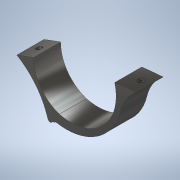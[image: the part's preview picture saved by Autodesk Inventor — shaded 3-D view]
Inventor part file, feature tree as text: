
AUTODESK INVENTOR PART (.ipt)
format: ipt  version: 2021 (Build 250183000, 183)  size: 151,040 bytes
history: native  units: in
note: dims shown in document units (in); Inventor stores cm internally (conversion verified against a paired STEP export)
features: extrude x3, plane x2, thread x2, other x1, sketch x1
ambient origin geometry x8: Origin, YZ Plane, XZ Plane, XY Plane, X Axis, Y Axis, Z Axis, Center Point
bodies: Solid1 (feature_tree)
feature tree (9):
  extrude  "Extrusion1"  Depth=0.3937in
  plane  "Work Plane1"
  extrude  "Extrusion2"  Depth=0.3937in TaperAngle=0.0deg
  thread  "Thread1"  [1 undecoded]
  plane  "Work Plane2"
  extrude  "Extrusion3"  Depth=0.3937in
  thread  "Thread2"  [1 undecoded]
  other  "Eixo de trabalho1"
  sketch  "Sketch1"  dims[d0=0.3535in d1=0.0in d2=0.0787in d3=0.3563in d4=0.0in d5=0.3937in d6=0.0in d7=0.0787in d8=0.3563in d9=0.0in d10=0.3937in d11=0.0in d12=0.1181in d13=0.1781in d14=0.3535in d15=0.1781in d16=0.1106in]
note: 2 required parameter values undecoded (feature->parameter linkage not recoverable at this tier; creation-order binding heuristic only, values carry confidence <= 0.55)
